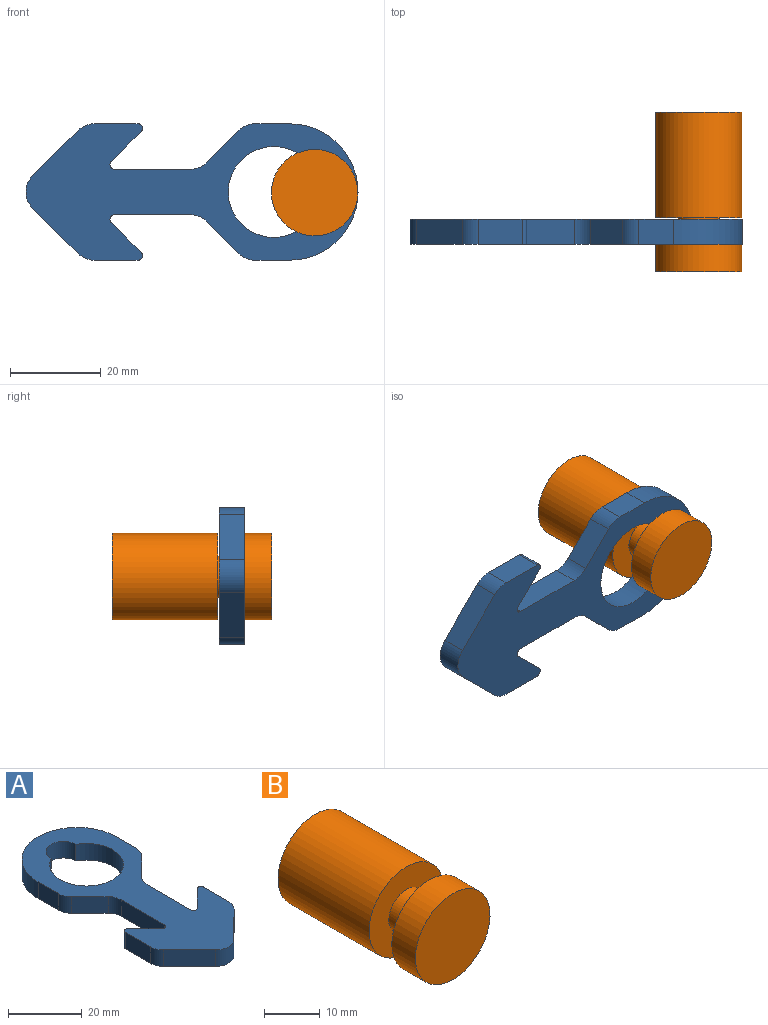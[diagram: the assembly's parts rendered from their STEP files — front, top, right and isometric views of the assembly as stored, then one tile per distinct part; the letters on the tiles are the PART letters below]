
ASSEMBLY  parts=2 mates=1
PART A: 28 faces, bbox 30x73x5.5 mm
  f0: plane 7.69x5.5mm, normal (-1,0,0), area 42.3mm2, adj f14,f15,f16,f17
  f1: plane 7.07x7.07mm, normal (-0.71,-0.71,0), area 55mm2, adj f15,f16,f17,f18
  f2: plane 16.73x5.5mm, normal (-1,0,0), area 92mm2, adj f15,f16,f18,f24
  f3: plane 6.59x6.59mm, normal (0.71,0.71,0), area 51.2mm2, adj f15,f16,f24,f25
  f4: plane 9.66x5.5mm, normal (-1,0,0), area 53.1mm2, adj f15,f16,f19,f25
  f5: plane 10x10mm, normal (-0.71,-0.71,0), area 77.8mm2, adj f15,f16,f19,f20
  f6: plane 10x10mm, normal (0.71,-0.71,0), area 77.8mm2, adj f15,f16,f20,f21
  f7: plane 9.66x5.5mm, normal (1,0,0), area 53.1mm2, adj f15,f16,f21,f26
  f8: plane 6.59x6.59mm, normal (-0.71,0.71,0), area 51.2mm2, adj f15,f16,f26,f27
  f9: plane 16.73x5.5mm, normal (1,0,0), area 92mm2, adj f15,f16,f22,f27
  f10: plane 7.07x7.07mm, normal (0.71,-0.71,0), area 55mm2, adj f15,f16,f22,f23
  f11: plane 7.69x5.5mm, normal (1,0,0), area 42.3mm2, adj f14,f15,f16,f23
  f12: cylinder r=4.75mm len=9.5mm, axis (0,0,-1), area 82.1mm2, adj f13,f15,f16
  f13: cylinder r=10mm len=20mm, axis (0,0,-1), area 291.1mm2, adj f12,f15,f16
  f14: cylinder r=15mm len=30mm, axis (0,0,-1), area 259.2mm2, adj f0,f11,f15,f16
  f15: plane 73.05x30mm, normal (0,0,1), area 1159.4mm2, adj f0,f1,f2,f3,f4,f5,f6,f7
  f16: plane 73.05x30mm, normal (0,0,-1), area 1159.4mm2, adj f0,f1,f2,f3,f4,f5,f6,f7
  f17: cylinder r=5mm len=5.5mm, axis (0,0,-1), area 21.6mm2, adj f0,f1,f15,f16
  f18: cylinder r=5mm len=5.5mm, axis (0,0,1), area 21.6mm2, adj f1,f2,f15,f16
  f19: cylinder r=5mm len=5.5mm, axis (0,0,-1), area 21.6mm2, adj f4,f5,f15,f16
  f20: cylinder r=5mm len=7.07mm, axis (0,0,1), area 43.2mm2, adj f5,f6,f15,f16
  f21: cylinder r=5mm len=5.5mm, axis (0,0,-1), area 21.6mm2, adj f6,f7,f15,f16
  f22: cylinder r=5mm len=5.5mm, axis (0,0,1), area 21.6mm2, adj f9,f10,f15,f16
  f23: cylinder r=5mm len=5.5mm, axis (0,0,-1), area 21.6mm2, adj f10,f11,f15,f16
  f24: cylinder r=1mm len=5.5mm, axis (0,0,1), area 13mm2, adj f2,f3,f15,f16
  f25: cylinder r=1mm len=5.5mm, axis (0,0,-1), area 13mm2, adj f3,f4,f15,f16
  f26: cylinder r=1mm len=5.5mm, axis (0,0,-1), area 13mm2, adj f7,f8,f15,f16
  f27: cylinder r=1mm len=5.5mm, axis (0,0,1), area 13mm2, adj f8,f9,f15,f16
PART B: 7 faces, bbox 19x35x19 mm
  f0: plane 19x19mm, normal (0,-1,0), area 283.5mm2, adj f6
  f1: plane 19x19mm, normal (0,1,0), area 283.5mm2, adj f2
  f2: cylinder r=9.5mm len=23.2mm, axis (0,1,0), area 1384.8mm2, adj f1,f3
  f3: plane 19x19mm, normal (0,-1,0), area 219.9mm2, adj f2,f4
  f4: cylinder r=4.5mm len=9mm, axis (0,1,0), area 164mm2, adj f3,f5
  f5: plane 19x19mm, normal (0,1,0), area 219.9mm2, adj f4,f6
  f6: cylinder r=9.5mm len=19mm, axis (0,1,0), area 358.1mm2, adj f0,f5
PLACE A rot(axis=(0.58,0.58,-0.58),120deg) t=(-0.21,11.5,0.13)mm
PLACE B at identity fixed
MATE planar A.f23 <-> B.f2  axis (0,-1,0) through (-13.16,6,-9.87)mm
